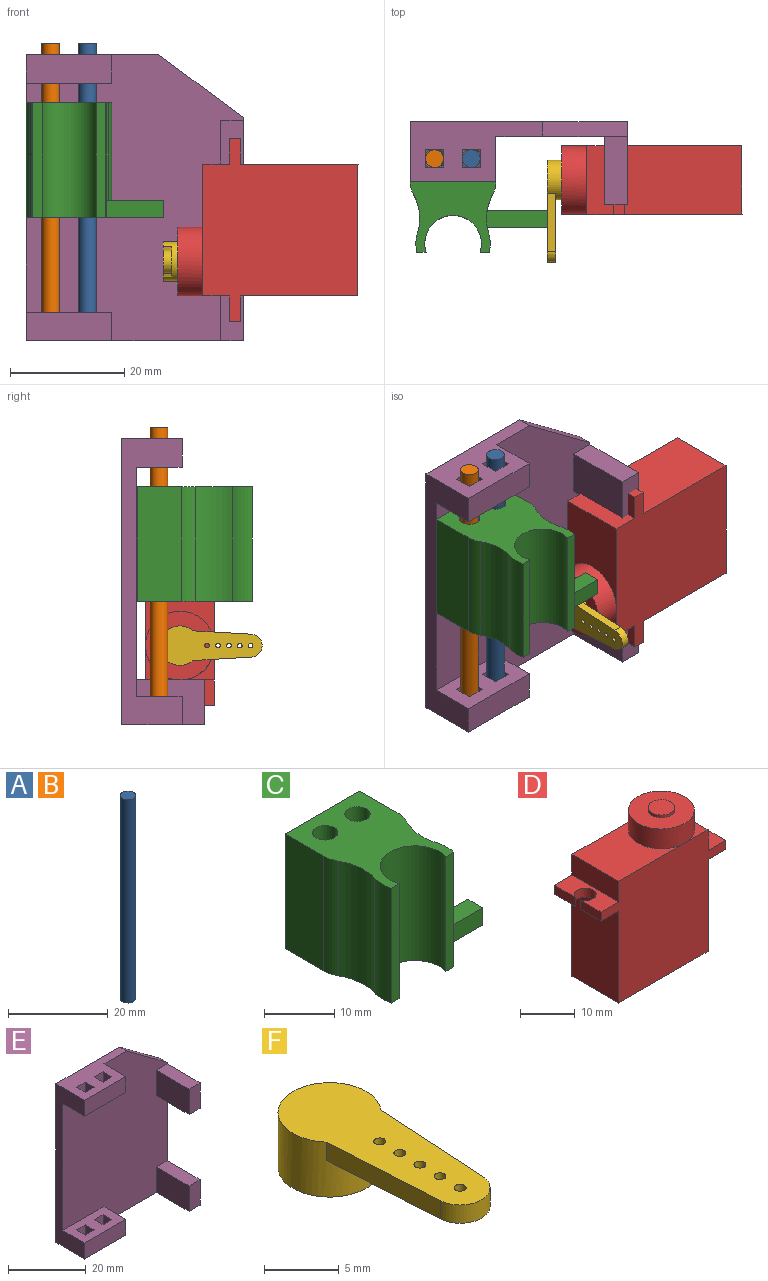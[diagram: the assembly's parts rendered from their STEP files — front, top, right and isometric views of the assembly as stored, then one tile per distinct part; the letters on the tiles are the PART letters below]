
ASSEMBLY  parts=6 mates=4
PART A: 3 faces, bbox 3.1x3.1x50 mm
  f0: cylinder r=1.55mm len=50mm, axis (0,0,-1), area 486.9mm2, adj f1,f2
  f1: plane 3.1x3.1mm, normal (0,0,1), area 7.5mm2, adj f0
  f2: plane 3.1x3.1mm, normal (0,0,-1), area 7.5mm2, adj f0
PART B: same geometry as A
PART C: 20 faces, bbox 24x20.1x20 mm
  f0: plane 20x7.71mm, normal (-1,0,0), area 154.2mm2, adj f1,f13,f14,f15
  f1: cylinder r=5mm len=20mm, axis (0,0,-1), area 50.2mm2, adj f0,f2,f14,f15
  f2: cylinder r=8.5mm len=20mm, axis (0,0,-1), area 136.4mm2, adj f1,f3,f14,f15
  f3: cylinder r=6.5mm len=20mm, axis (0,0,-1), area 69mm2, adj f2,f4,f14,f15
  f4: plane 20x1.61mm, normal (0,-1,0), area 32.1mm2, adj f3,f5,f14,f15
  f5: cylinder r=4.95mm len=20mm, axis (0,0,-1), area 371.5mm2, adj f4,f6,f14,f15
  f6: plane 20x1.61mm, normal (0,-1,0), area 32.1mm2, adj f5,f7,f14,f15
  f7: cylinder r=6.5mm len=20mm, axis (0,0,-1), area 69mm2, adj f6,f8,f14,f15
  f8: cylinder r=8.5mm len=20mm, axis (0,0,-1), area 127.4mm2, adj f7,f9,f14,f15,f16,f18,f19
  f9: cylinder r=5mm len=20mm, axis (0,0,-1), area 50.2mm2, adj f8,f10,f14,f15
  f10: plane 20x7.71mm, normal (1,0,0), area 154.2mm2, adj f9,f13,f14,f15
  f11: cylinder r=1.8mm len=20mm, axis (0,0,-1), area 226.2mm2, adj f14,f15
  f12: cylinder r=1.8mm len=20mm, axis (0,0,-1), area 226.2mm2, adj f14,f15
  f13: plane 20x15mm, normal (0,1,0), area 300mm2, adj f0,f10,f14,f15
  f14: plane 20.13x15mm, normal (0,0,1), area 201.7mm2, adj f0,f1,f2,f3,f4,f5,f6,f7
  f15: plane 24x20.13mm, normal (0,0,-1), area 233.6mm2, adj f0,f1,f2,f3,f4,f5,f6,f7
  f16: plane 10.52x3mm, normal (0,-1,0), area 31.6mm2, adj f8,f15,f17,f18
  f17: plane 3x3mm, normal (1,0,0), area 9mm2, adj f15,f16,f18,f19
  f18: plane 10.67x3mm, normal (0,0,1), area 31.9mm2, adj f8,f16,f17,f19
  f19: plane 10.55x3mm, normal (0,1,0), area 31.6mm2, adj f8,f15,f17,f18
PART D: 24 faces, bbox 32x12x32.1 mm
  f0: plane 6x6mm, normal (0,0,1), area 7.7mm2, adj f3,f4,f20
  f1: plane 17x12mm, normal (0,0,1), area 147.5mm2, adj f2,f4,f6,f20
  f2: plane 12x4.6mm, normal (-1,0,0), area 55.2mm2, adj f1,f4,f6,f18
  f3: plane 12x4.6mm, normal (1,0,0), area 55.2mm2, adj f0,f4,f6,f9,f13
  f4: plane 32x27.1mm, normal (0,-1,0), area 641.3mm2, adj f0,f1,f2,f3,f5,f7,f8,f10
  f5: plane 20.5x12mm, normal (1,0,0), area 246mm2, adj f4,f6,f8,f14
  f6: plane 32x27.1mm, normal (0,1,0), area 641.3mm2, adj f1,f2,f3,f5,f7,f8,f9,f12
  f7: plane 20.5x12mm, normal (-1,0,0), area 246mm2, adj f4,f6,f8,f19
  f8: plane 23x12mm, normal (0,0,-1), area 276mm2, adj f4,f5,f6,f7
  f9: plane 6x6mm, normal (0,0,1), area 7.7mm2, adj f3,f6,f20
  f10: plane 5.38x2mm, normal (1,0,0), area 10.8mm2, adj f4,f11,f13,f14
  f11: cylinder r=2mm len=4mm, axis (0,0,-1), area 22.6mm2, adj f10,f12,f13,f14
  f12: plane 5.38x2mm, normal (1,0,0), area 10.8mm2, adj f6,f11,f13,f14
  f13: plane 12x4.5mm, normal (0,0,1), area 41.5mm2, adj f3,f4,f6,f10,f11,f12
  f14: plane 12x4.5mm, normal (0,0,-1), area 41.5mm2, adj f4,f5,f6,f10,f11,f12
  f15: plane 5.38x2mm, normal (-1,0,0), area 10.8mm2, adj f6,f16,f18,f19
  f16: cylinder r=2mm len=4mm, axis (0,0,-1), area 22.6mm2, adj f15,f17,f18,f19
  f17: plane 5.38x2mm, normal (-1,0,0), area 10.8mm2, adj f4,f16,f18,f19
  f18: plane 12x4.5mm, normal (0,0,1), area 41.5mm2, adj f2,f4,f6,f15,f16,f17
  f19: plane 12x4.5mm, normal (0,0,-1), area 41.5mm2, adj f4,f6,f7,f15,f16,f17
  f20: cylinder r=6mm len=12mm, axis (0,0,-1), area 165.9mm2, adj f0,f1,f9,f21
  f21: plane 12x12mm, normal (0,0,1), area 94.6mm2, adj f20,f22
  f22: cylinder r=2.43mm len=4.85mm, axis (0,0,-1), area 9.1mm2, adj f21,f23
  f23: plane 4.85x4.85mm, normal (0,0,1), area 18.5mm2, adj f22
PART E: 38 faces, bbox 38x14.5x50 mm
  f0: plane 50x38mm, normal (0,-1,0), area 1604.3mm2, adj f8,f9,f10,f11,f12,f23,f24,f26
  f1: plane 3.2x3mm, normal (1,0,0), area 9.6mm2, adj f2,f3,f28,f30
  f2: plane 3.2x3mm, normal (0,-1,0), area 9.6mm2, adj f1,f4,f28,f30
  f3: plane 3.2x3mm, normal (0,1,0), area 9.6mm2, adj f1,f4,f28,f30
  f4: plane 3.2x3mm, normal (-1,0,0), area 9.6mm2, adj f2,f3,f28,f30
  f5: plane 3.2x3mm, normal (0,1,0), area 9.6mm2, adj f6,f25,f28,f29
  f6: plane 3.2x3mm, normal (-1,0,0), area 9.6mm2, adj f5,f7,f28,f29
  f7: plane 3.2x3mm, normal (0,-1,0), area 9.6mm2, adj f6,f25,f28,f29
  f8: plane 23.17x10.5mm, normal (0,0,1), area 157.5mm2, adj f0,f9,f12,f13,f14,f15,f16,f17
  f9: plane 50x10.5mm, normal (-1,0,0), area 205mm2, adj f0,f8,f10,f13,f14,f24,f27,f28
  f10: plane 38x14.5mm, normal (0,0,-1), area 263mm2, adj f0,f9,f11,f13,f26,f27,f32,f33
  f11: plane 38.97x14.5mm, normal (1,0,0), area 289.4mm2, adj f0,f10,f12,f13,f31,f33,f35,f36
  f12: plane 14.83x11.03mm, normal (0.6,0,0.8), area 46.2mm2, adj f0,f8,f11,f13
  f13: plane 50x38mm, normal (0,1,0), area 1818.3mm2, adj f8,f9,f10,f11,f12
  f14: plane 15x5mm, normal (0,-1,0), area 75mm2, adj f8,f9,f23,f24
  f15: plane 5x3.2mm, normal (1,0,0), area 16mm2, adj f8,f16,f21,f24
  f16: plane 5x3.2mm, normal (0,-1,0), area 16mm2, adj f8,f15,f17,f24
  f17: plane 5x3.2mm, normal (-1,0,0), area 16mm2, adj f8,f16,f21,f24
  f18: plane 5x3.2mm, normal (0,-1,0), area 16mm2, adj f8,f19,f22,f24
  f19: plane 5x3.2mm, normal (-1,0,0), area 16mm2, adj f8,f18,f20,f24
  f20: plane 5x3.2mm, normal (0,1,0), area 16mm2, adj f8,f19,f22,f24
  f21: plane 5x3.2mm, normal (0,1,0), area 16mm2, adj f8,f15,f17,f24
  f22: plane 5x3.2mm, normal (1,0,0), area 16mm2, adj f8,f18,f20,f24
  f23: plane 8x5mm, normal (1,0,0), area 40mm2, adj f0,f8,f14,f24
  f24: plane 15x8mm, normal (0,0,-1), area 99.5mm2, adj f0,f9,f14,f15,f16,f17,f18,f19
  f25: plane 3.2x3mm, normal (1,0,0), area 9.6mm2, adj f5,f7,f28,f29
  f26: plane 8x5mm, normal (1,0,0), area 40mm2, adj f0,f10,f27,f28
  f27: plane 15x5mm, normal (0,-1,0), area 75mm2, adj f9,f10,f26,f28
  f28: plane 15x8mm, normal (0,0,1), area 99.5mm2, adj f0,f1,f2,f3,f4,f5,f6,f7
  f29: plane 3.2x3.2mm, normal (0,0,1), area 10.2mm2, adj f5,f6,f7,f25
  f30: plane 3.2x3.2mm, normal (0,0,1), area 10.2mm2, adj f1,f2,f3,f4
  f31: plane 12x4mm, normal (0,0,1), area 48mm2, adj f0,f11,f32,f33
  f32: plane 12x8mm, normal (-1,0,0), area 96mm2, adj f0,f10,f31,f33
  f33: plane 8x4mm, normal (0,-1,0), area 32mm2, adj f10,f11,f31,f32
  f34: plane 12x8mm, normal (-1,0,0), area 96mm2, adj f0,f35,f36,f37
  f35: plane 12x4mm, normal (0,0,-1), area 48mm2, adj f0,f11,f34,f37
  f36: plane 12x4mm, normal (0,0,1), area 48mm2, adj f0,f11,f34,f37
  f37: plane 8x4mm, normal (0,-1,0), area 32mm2, adj f11,f34,f35,f36
PART F: 14 faces, bbox 6.9x17.8x4.5 mm
  f0: cylinder r=2.43mm len=4.85mm, axis (0,0,1), area 39.6mm2, adj f2,f3
  f1: cylinder r=3.45mm len=6.9mm, axis (0,0,1), area 88.7mm2, adj f2,f4,f5,f12,f13
  f2: plane 6.9x6.9mm, normal (0,0,-1), area 18.9mm2, adj f0,f1
  f3: plane 4.85x4.85mm, normal (0,0,-1), area 18.5mm2, adj f0
  f4: plane 17.8x6.9mm, normal (0,0,1), area 83.3mm2, adj f1,f5,f6,f7,f8,f9,f10,f11
  f5: plane 10.2x1.5mm, normal (-1,-0.06,0), area 15.3mm2, adj f1,f4,f6,f13
  f6: cylinder r=2mm len=3.99mm, axis (0,0,-1), area 9.1mm2, adj f4,f5,f12,f13
  f7: cylinder r=0.4mm len=1.5mm, axis (0,0,-1), area 3.8mm2, adj f4,f13
  f8: cylinder r=0.4mm len=1.5mm, axis (0,0,-1), area 3.8mm2, adj f4,f13
  f9: cylinder r=0.4mm len=1.5mm, axis (0,0,-1), area 3.8mm2, adj f4,f13
  f10: cylinder r=0.4mm len=1.5mm, axis (0,0,-1), area 3.8mm2, adj f4,f13
  f11: cylinder r=0.4mm len=1.5mm, axis (0,0,-1), area 3.8mm2, adj f4,f13
  f12: plane 10.2x1.5mm, normal (1,-0.06,0), area 15.3mm2, adj f1,f4,f6,f13
  f13: plane 12.08x5.2mm, normal (0,0,-1), area 45.9mm2, adj f1,f5,f6,f7,f8,f9,f10,f11
PLACE A rot(axis=(-0.05,0.98,0.18),0deg) t=(65.52,35.84,7.19)mm
PLACE B rot(axis=(-0.05,0.98,0.18),0deg) t=(59.07,35.84,7.19)mm
PLACE C rot(axis=(-0.05,0.98,0.18),0deg) t=(26.89,4.58,26.78)mm
PLACE D rot(axis=(0.71,0,-0.71),180deg) t=(47.67,11.95,19.02)mm
PLACE E rot(axis=(-0.05,0.98,0.18),0deg) t=(59.65,22.08,66.07)mm
PLACE F rot(axis=(0,-1,0),90deg) t=(47.67,11.95,19.02)mm
MATE fastened E.f29 <-> A.f0  axis (0,0,1) through (20.89,15.63,7.19)mm
MATE fastened E.f30 <-> B.f0  axis (0,0,1) through (14.44,15.63,7.19)mm
MATE revolute F.f0 <-> D.f20  axis (1,0,0) through (36.07,11.95,19.02)mm
MATE slider C.f11 <-> B.f0  axis (0,0,1) through (14.44,15.63,46.78)mm
